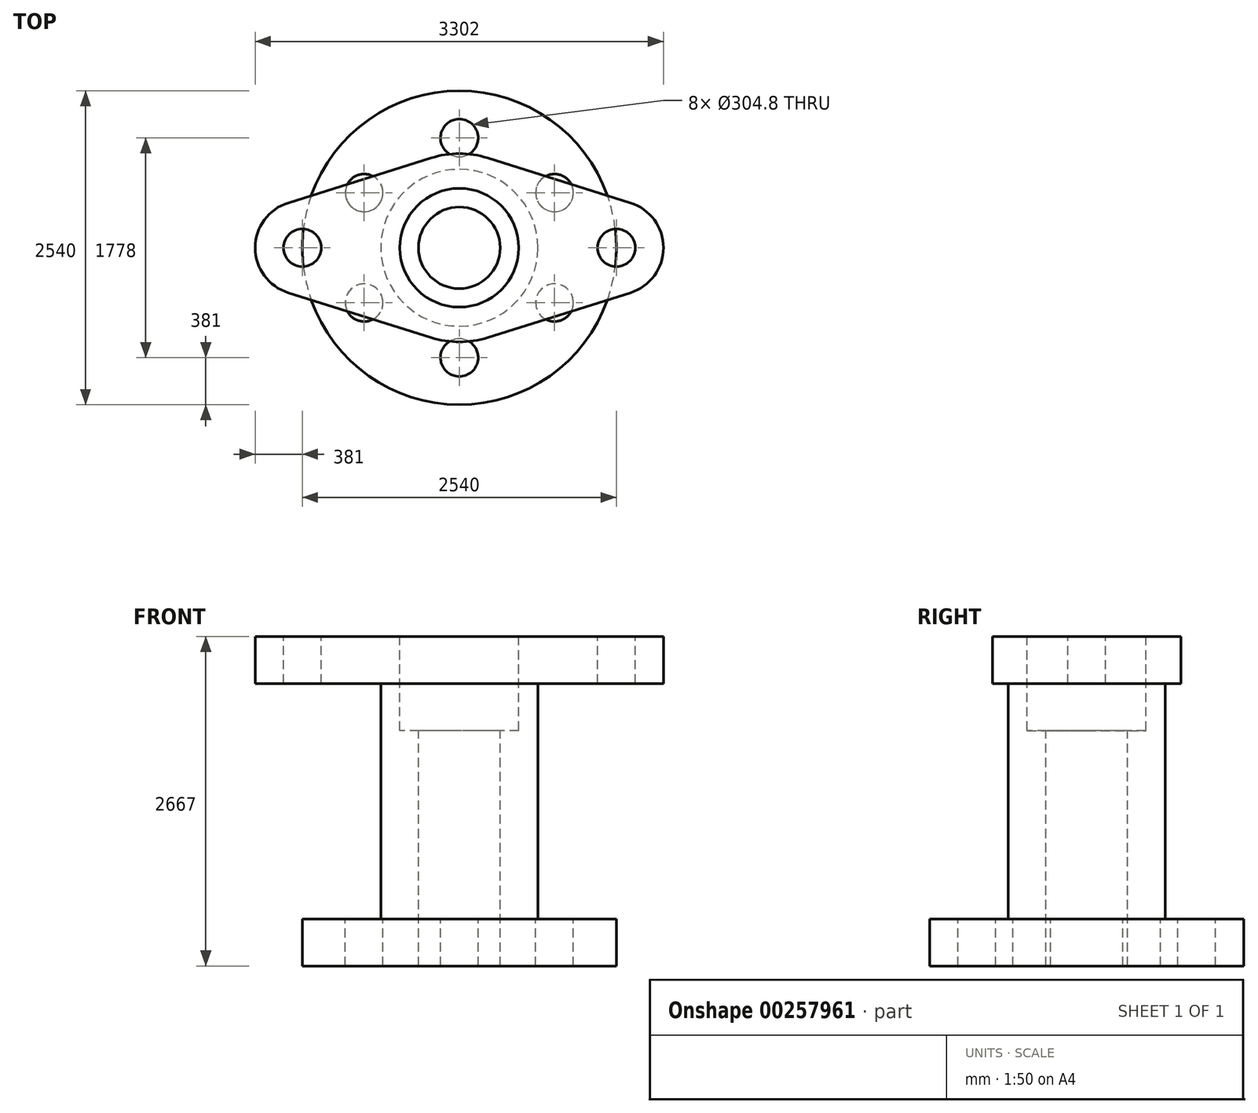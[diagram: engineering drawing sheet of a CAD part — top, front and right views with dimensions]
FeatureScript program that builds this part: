
annotation { "Feature Type Name" : "Feature", "Feature Type Description" : "" }
export const myFeature = defineFeature(function(context is Context, id is Id, definition is map)
    precondition{}
    {
        {
            var Q0;
            Q0=qCreatedBy(makeId("Top.planeOp"),FACE);
            var sketch = newSketch(context, id + "F0", { "sketchPlane" : qUnion([Q0])});
            skCircle(sketch, "E0", {"center": v(0, 0) * mm, "radius": 1270 * mm});
            skLineSegment(sketch, "E1", {"start": v(0, 2113.44) * mm, "end": v(0, -2948.36) * mm, "construction": true});
            skLineSegment(sketch, "E2", {"start": v(-1801.59, 0) * mm, "end": v(2508.96, 0) * mm, "construction": true});
            skCircle(sketch, "E3", {"center": v(0, 0) * mm, "radius": 889 * mm, "construction": true});
            skCircle(sketch, "E4", {"center": v(0, 889) * mm, "radius": 152.4 * mm});
            skCircle(sketch, "E5.MirrorC", {"center": v(0, -889) * mm, "radius": 152.4 * mm});
            skCircle(sketch, "E6.1.0", {"center": v(-769.9, 444.5) * mm, "radius": 152.4 * mm});
            skCircle(sketch, "E6.2.0", {"center": v(-769.9, -444.5) * mm, "radius": 152.4 * mm});
            skCircle(sketch, "E6.4.0", {"center": v(769.9, -444.5) * mm, "radius": 152.4 * mm});
            skCircle(sketch, "E6.5.0", {"center": v(769.9, 444.5) * mm, "radius": 152.4 * mm});
            skSolve(sketch);
        }
        {
            var Q0;
            Q0 = qSketchRegion(id + "F0", true);
            extrude(context, id + "F1", {"entities" : qUnion([Q0]), "oppositeDirection" : true, "depth" : 381 * mm});
        }
        {
            var Q0;
            Q0=makeQuery(id+"F1.opExtrude","CAP_FACE",FACE,{"disambiguationData":[OSD([sQuery(id+"F0.wireOp",EDGE,"E0"),sQuery(id+"F0.wireOp",EDGE,"E4"),sQuery(id+"F0.wireOp",EDGE,"E6.1.0"),sQuery(id+"F0.wireOp",EDGE,"E6.2.0"),sQuery(id+"F0.wireOp",EDGE,"E5.MirrorC"),sQuery(id+"F0.wireOp",EDGE,"E6.4.0"),sQuery(id+"F0.wireOp",EDGE,"E6.5.0")])],"isStart":true});
            var sketch = newSketch(context, id + "F2", { "sketchPlane" : qUnion([Q0])});
            skCircle(sketch, "E7", {"center": v(0, 0) * mm, "radius": 635 * mm});
            skSolve(sketch);
        }
        {
            var Q0;
            Q0 = qSketchRegion(id + "F2", true);
            extrude(context, id + "F3", {"entities" : qUnion([Q0]), "operationType" : NewBodyOperationType.ADD, "depth" : 1905 * mm});
        }
        {
            var Q0;
            Q0=makeQuery(id+"F3.opExtrude","CAP_FACE",FACE,{"disambiguationData":[OSD([sQuery(id+"F2.wireOp",EDGE,"E7")])],"isStart":false});
            var sketch = newSketch(context, id + "F4", { "sketchPlane" : qUnion([Q0])});
            skLineSegment(sketch, "E8", {"start": v(-1584.1, 0) * mm, "end": v(1877.76, 0) * mm, "construction": true});
            skArc(sketch, "E9", {"start": v(1340.62, -374.4) * mm, "mid": v(1651, -1.12) * mm, "end": v(1342.82, 373.98) * mm});
            skLineSegment(sketch, "E10", {"start": v(0, 1881.61) * mm, "end": v(0, -2662.07) * mm, "construction": true});
            skArc(sketch, "E11.MirrorCS", {"start": v(-1340.62, -374.4) * mm, "mid": v(-1651, -1.12) * mm, "end": v(-1342.82, 373.98) * mm});
            skCircle(sketch, "E12", {"center": v(0, 0) * mm, "radius": 762 * mm});
            skLineSegment(sketch, "E13", {"start": v(228.6, 726.9) * mm, "end": v(1384.3, 363.45) * mm});
            skLineSegment(sketch, "E14", {"start": v(228.6, -726.9) * mm, "end": v(1384.3, -363.45) * mm});
            skLineSegment(sketch, "E15", {"start": v(-1384.3, 363.45) * mm, "end": v(-228.6, 726.9) * mm});
            skLineSegment(sketch, "E16.MirrorCS", {"start": v(-228.6, -726.9) * mm, "end": v(-1384.3, -363.45) * mm});
            skSolve(sketch);
        }
        {
            var Q0;
            Q0 = qSketchRegion(id + "F4", true);
            extrude(context, id + "F5", {"entities" : qUnion([Q0]), "operationType" : NewBodyOperationType.ADD, "depth" : 381 * mm});
        }
        {
            var Q0;
            Q0 = qSketchRegion(id + "F4", true);
            extrude(context, id + "F6", {"entities" : qUnion([Q0]), "operationType" : NewBodyOperationType.ADD, "depth" : 381 * mm});
        }
        {
            var Q0;
            Q0=makeQuery(id+"F5.opExtrude","CAP_FACE",FACE,{"disambiguationData":[OSD([sQuery(id+"F4.wireOp",EDGE,"E9"),sQuery(id+"F4.wireOp",EDGE,"E11.MirrorCS"),sQuery(id+"F4.wireOp",EDGE,"E12"),sQuery(id+"F4.wireOp",EDGE,"E13"),sQuery(id+"F4.wireOp",EDGE,"E14"),sQuery(id+"F4.wireOp",EDGE,"E15"),sQuery(id+"F4.wireOp",EDGE,"E16.MirrorCS")])],"isStart":false});
            var sketch = newSketch(context, id + "F7", { "sketchPlane" : qUnion([Q0])});
            skLineSegment(sketch, "E17", {"start": v(-2701.7, 0) * mm, "end": v(3133.6, 0) * mm, "construction": true});
            skCircle(sketch, "E18", {"center": v(0, 0) * mm, "radius": 330.2 * mm});
            skSolve(sketch);
        }
        {
            var Q0;
            Q0 = qSketchRegion(id + "F7", true);
            extrude(context, id + "F8", {"entities" : qUnion([Q0]), "operationType" : NewBodyOperationType.REMOVE, "oppositeDirection" : true, "depth" : 2667 * mm});
        }
        {
            var Q0;
            Q0=makeQuery(id+"F5.opExtrude","CAP_FACE",FACE,{"disambiguationData":[OSD([sQuery(id+"F4.wireOp",EDGE,"E9"),sQuery(id+"F4.wireOp",EDGE,"E11.MirrorCS"),sQuery(id+"F4.wireOp",EDGE,"E12"),sQuery(id+"F4.wireOp",EDGE,"E13"),sQuery(id+"F4.wireOp",EDGE,"E14"),sQuery(id+"F4.wireOp",EDGE,"E15"),sQuery(id+"F4.wireOp",EDGE,"E16.MirrorCS")])],"isStart":false});
            var sketch = newSketch(context, id + "F9", { "sketchPlane" : qUnion([Q0])});
            skCircle(sketch, "E19", {"center": v(0, 0) * mm, "radius": 480.6 * mm});
            skSolve(sketch);
        }
        {
            var Q0;
            Q0 = qSketchRegion(id + "F9", true);
            extrude(context, id + "F10", {"entities" : qUnion([Q0]), "operationType" : NewBodyOperationType.REMOVE, "oppositeDirection" : true, "depth" : 762 * mm});
        }
        {
            var Q0;
            Q0=makeQuery(id+"F5.opExtrude","CAP_FACE",FACE,{"disambiguationData":[OSD([sQuery(id+"F4.wireOp",EDGE,"E9"),sQuery(id+"F4.wireOp",EDGE,"E11.MirrorCS"),sQuery(id+"F4.wireOp",EDGE,"E12"),sQuery(id+"F4.wireOp",EDGE,"E13"),sQuery(id+"F4.wireOp",EDGE,"E14"),sQuery(id+"F4.wireOp",EDGE,"E15"),sQuery(id+"F4.wireOp",EDGE,"E16.MirrorCS")])],"isStart":false});
            var sketch = newSketch(context, id + "F11", { "sketchPlane" : qUnion([Q0])});
            skLineSegment(sketch, "E20", {"start": v(-2574.72, 0) * mm, "end": v(2974.01, 0) * mm, "construction": true});
            skPoint(sketch, "E20.endSnap0", {"position": v(1651, 0) * mm});
            skLineSegment(sketch, "E21", {"start": v(0, 1717.63) * mm, "end": v(0, -2013.65) * mm, "construction": true});
            skCircle(sketch, "E22", {"center": v(1270, 0) * mm, "radius": 152.4 * mm});
            skCircle(sketch, "E23", {"center": v(-1270, 0) * mm, "radius": 152.4 * mm});
            skSolve(sketch);
        }
        {
            var Q0;
            Q0 = qSketchRegion(id + "F11", true);
            extrude(context, id + "F12", {"entities" : qUnion([Q0]), "operationType" : NewBodyOperationType.REMOVE, "oppositeDirection" : true, "depth" : 381 * mm});
        }
    });
